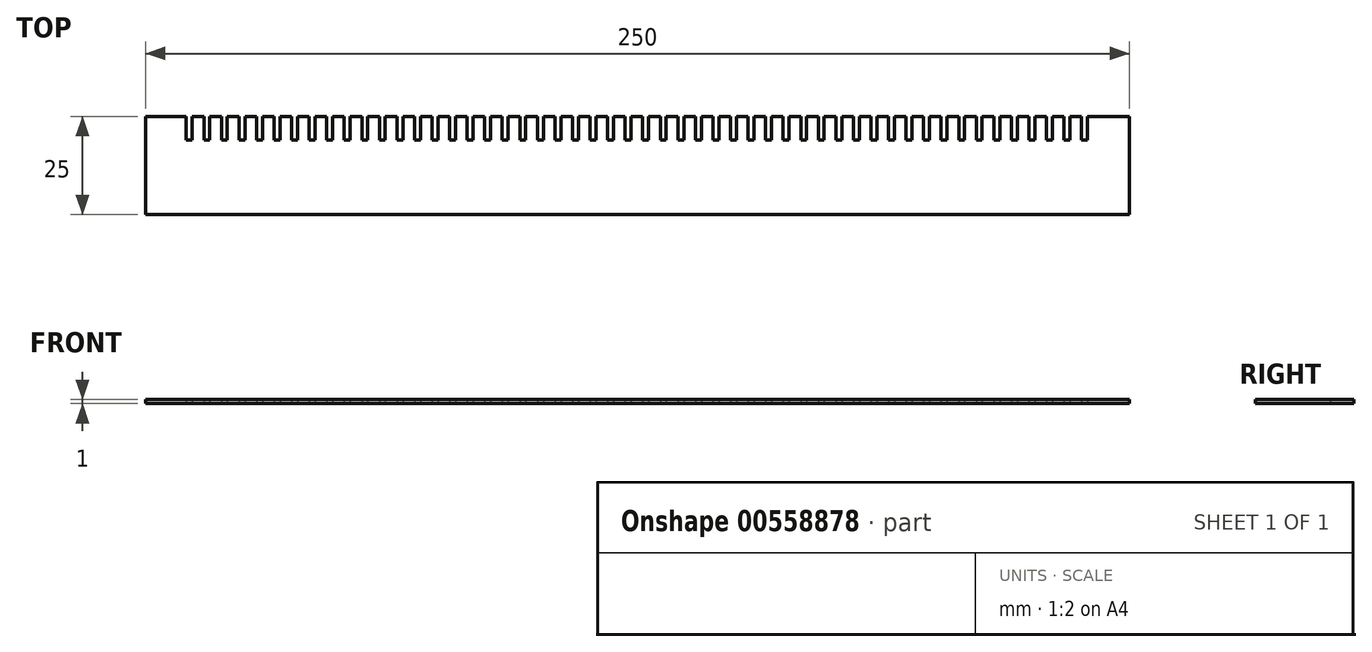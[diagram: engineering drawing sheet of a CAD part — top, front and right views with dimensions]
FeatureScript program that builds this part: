
annotation { "Feature Type Name" : "Feature", "Feature Type Description" : "" }
export const myFeature = defineFeature(function(context is Context, id is Id, definition is map)
    precondition{}
    {
        {
            var Q0;
            Q0=qCreatedBy(makeId("Top.planeOp"),FACE);
            var sketch = newSketch(context, id + "F0", { "sketchPlane" : qUnion([Q0])});
            skLineSegment(sketch, "E0.bottom", {"start": v(-82.75, 53.01) * mm, "end": v(-72.35, 53.01) * mm});
            skLineSegment(sketch, "E0.top", {"start": v(-82.75, 28.01) * mm, "end": v(167.25, 28.01) * mm});
            skLineSegment(sketch, "E0.left", {"start": v(-82.75, 53.01) * mm, "end": v(-82.75, 28.01) * mm});
            skLineSegment(sketch, "E0.right", {"start": v(167.25, 53.01) * mm, "end": v(167.25, 28.01) * mm});
            skLineSegment(sketch, "E1.top", {"start": v(-72.35, 47.01) * mm, "end": v(-70.85, 47.01) * mm});
            skLineSegment(sketch, "E1.left", {"start": v(-72.35, 53.01) * mm, "end": v(-72.35, 47.01) * mm});
            skLineSegment(sketch, "E1.right", {"start": v(-70.85, 53.01) * mm, "end": v(-70.85, 47.01) * mm});
            skLineSegment(sketch, "E2.trimOffspring", {"start": v(-70.85, 53.01) * mm, "end": v(-67.9, 53.01) * mm});
            skLineSegment(sketch, "E3.1.0.0", {"start": v(-67.9, 47.01) * mm, "end": v(-66.4, 47.01) * mm});
            skLineSegment(sketch, "E3.1.0.1", {"start": v(-67.9, 53.01) * mm, "end": v(-67.9, 47.01) * mm});
            skLineSegment(sketch, "E3.1.0.2", {"start": v(-66.4, 53.01) * mm, "end": v(-66.4, 47.01) * mm});
            skLineSegment(sketch, "E3.2.0.0", {"start": v(-63.43, 47.01) * mm, "end": v(-61.93, 47.01) * mm});
            skLineSegment(sketch, "E3.2.0.1", {"start": v(-63.43, 53.01) * mm, "end": v(-63.43, 47.01) * mm});
            skLineSegment(sketch, "E3.2.0.2", {"start": v(-61.93, 53.01) * mm, "end": v(-61.93, 47.01) * mm});
            skLineSegment(sketch, "E3.3.0.0", {"start": v(-58.97, 47.01) * mm, "end": v(-57.47, 47.01) * mm});
            skLineSegment(sketch, "E3.3.0.1", {"start": v(-58.97, 53.01) * mm, "end": v(-58.97, 47.01) * mm});
            skLineSegment(sketch, "E3.3.0.2", {"start": v(-57.47, 53.01) * mm, "end": v(-57.47, 47.01) * mm});
            skLineSegment(sketch, "E3.4.0.0", {"start": v(-54.51, 47.01) * mm, "end": v(-53.01, 47.01) * mm});
            skLineSegment(sketch, "E3.4.0.1", {"start": v(-54.51, 53.01) * mm, "end": v(-54.51, 47.01) * mm});
            skLineSegment(sketch, "E3.4.0.2", {"start": v(-53.01, 53.01) * mm, "end": v(-53.01, 47.01) * mm});
            skLineSegment(sketch, "E3.5.0.0", {"start": v(-50.05, 47.01) * mm, "end": v(-48.55, 47.01) * mm});
            skLineSegment(sketch, "E3.5.0.1", {"start": v(-50.05, 53.01) * mm, "end": v(-50.05, 47.01) * mm});
            skLineSegment(sketch, "E3.5.0.2", {"start": v(-48.55, 53.01) * mm, "end": v(-48.55, 47.01) * mm});
            skLineSegment(sketch, "E3.6.0.0", {"start": v(-45.6, 47.01) * mm, "end": v(-44.1, 47.01) * mm});
            skLineSegment(sketch, "E3.6.0.1", {"start": v(-45.6, 53.01) * mm, "end": v(-45.6, 47.01) * mm});
            skLineSegment(sketch, "E3.6.0.2", {"start": v(-44.1, 53.01) * mm, "end": v(-44.1, 47.01) * mm});
            skLineSegment(sketch, "E3.7.0.0", {"start": v(-41.13, 47.01) * mm, "end": v(-39.63, 47.01) * mm});
            skLineSegment(sketch, "E3.7.0.1", {"start": v(-41.13, 53.01) * mm, "end": v(-41.13, 47.01) * mm});
            skLineSegment(sketch, "E3.7.0.2", {"start": v(-39.63, 53.01) * mm, "end": v(-39.63, 47.01) * mm});
            skLineSegment(sketch, "E3.8.0.0", {"start": v(-36.67, 47.01) * mm, "end": v(-35.17, 47.01) * mm});
            skLineSegment(sketch, "E3.8.0.1", {"start": v(-36.67, 53.01) * mm, "end": v(-36.67, 47.01) * mm});
            skLineSegment(sketch, "E3.8.0.2", {"start": v(-35.17, 53.01) * mm, "end": v(-35.17, 47.01) * mm});
            skLineSegment(sketch, "E3.9.0.0", {"start": v(-32.21, 47.01) * mm, "end": v(-30.71, 47.01) * mm});
            skLineSegment(sketch, "E3.9.0.1", {"start": v(-32.21, 53.01) * mm, "end": v(-32.21, 47.01) * mm});
            skLineSegment(sketch, "E3.9.0.2", {"start": v(-30.71, 53.01) * mm, "end": v(-30.71, 47.01) * mm});
            skLineSegment(sketch, "E3.10.0.0", {"start": v(-27.75, 47.01) * mm, "end": v(-26.25, 47.01) * mm});
            skLineSegment(sketch, "E3.10.0.1", {"start": v(-27.75, 53.01) * mm, "end": v(-27.75, 47.01) * mm});
            skLineSegment(sketch, "E3.10.0.2", {"start": v(-26.25, 53.01) * mm, "end": v(-26.25, 47.01) * mm});
            skLineSegment(sketch, "E3.11.0.0", {"start": v(-23.3, 47.01) * mm, "end": v(-21.8, 47.01) * mm});
            skLineSegment(sketch, "E3.11.0.1", {"start": v(-23.3, 53.01) * mm, "end": v(-23.3, 47.01) * mm});
            skLineSegment(sketch, "E3.11.0.2", {"start": v(-21.8, 53.01) * mm, "end": v(-21.8, 47.01) * mm});
            skLineSegment(sketch, "E3.12.0.0", {"start": v(-18.83, 47.01) * mm, "end": v(-17.33, 47.01) * mm});
            skLineSegment(sketch, "E3.12.0.1", {"start": v(-18.83, 53.01) * mm, "end": v(-18.83, 47.01) * mm});
            skLineSegment(sketch, "E3.12.0.2", {"start": v(-17.33, 53.01) * mm, "end": v(-17.33, 47.01) * mm});
            skLineSegment(sketch, "E3.13.0.0", {"start": v(-14.37, 47.01) * mm, "end": v(-12.87, 47.01) * mm});
            skLineSegment(sketch, "E3.13.0.1", {"start": v(-14.37, 53.01) * mm, "end": v(-14.37, 47.01) * mm});
            skLineSegment(sketch, "E3.13.0.2", {"start": v(-12.87, 53.01) * mm, "end": v(-12.87, 47.01) * mm});
            skLineSegment(sketch, "E3.14.0.0", {"start": v(-9.91, 47.01) * mm, "end": v(-8.41, 47.01) * mm});
            skLineSegment(sketch, "E3.14.0.1", {"start": v(-9.91, 53.01) * mm, "end": v(-9.91, 47.01) * mm});
            skLineSegment(sketch, "E3.14.0.2", {"start": v(-8.41, 53.01) * mm, "end": v(-8.41, 47.01) * mm});
            skLineSegment(sketch, "E3.15.0.0", {"start": v(-5.45, 47.01) * mm, "end": v(-3.95, 47.01) * mm});
            skLineSegment(sketch, "E3.15.0.1", {"start": v(-5.45, 53.01) * mm, "end": v(-5.45, 47.01) * mm});
            skLineSegment(sketch, "E3.15.0.2", {"start": v(-3.95, 53.01) * mm, "end": v(-3.95, 47.01) * mm});
            skLineSegment(sketch, "E3.16.0.0", {"start": v(-1, 47.01) * mm, "end": v(0.5, 47.01) * mm});
            skLineSegment(sketch, "E3.16.0.1", {"start": v(-1, 53.01) * mm, "end": v(-1, 47.01) * mm});
            skLineSegment(sketch, "E3.16.0.2", {"start": v(0.5, 53.01) * mm, "end": v(0.5, 47.01) * mm});
            skLineSegment(sketch, "E3.17.0.0", {"start": v(3.47, 47.01) * mm, "end": v(4.97, 47.01) * mm});
            skLineSegment(sketch, "E3.17.0.1", {"start": v(3.47, 53.01) * mm, "end": v(3.47, 47.01) * mm});
            skLineSegment(sketch, "E3.17.0.2", {"start": v(4.97, 53.01) * mm, "end": v(4.97, 47.01) * mm});
            skLineSegment(sketch, "E3.18.0.0", {"start": v(7.93, 47.01) * mm, "end": v(9.43, 47.01) * mm});
            skLineSegment(sketch, "E3.18.0.1", {"start": v(7.93, 53.01) * mm, "end": v(7.93, 47.01) * mm});
            skLineSegment(sketch, "E3.18.0.2", {"start": v(9.43, 53.01) * mm, "end": v(9.43, 47.01) * mm});
            skLineSegment(sketch, "E3.19.0.0", {"start": v(12.39, 47.01) * mm, "end": v(13.89, 47.01) * mm});
            skLineSegment(sketch, "E3.19.0.1", {"start": v(12.39, 53.01) * mm, "end": v(12.39, 47.01) * mm});
            skLineSegment(sketch, "E3.19.0.2", {"start": v(13.89, 53.01) * mm, "end": v(13.89, 47.01) * mm});
            skLineSegment(sketch, "E3.20.0.0", {"start": v(16.85, 47.01) * mm, "end": v(18.35, 47.01) * mm});
            skLineSegment(sketch, "E3.20.0.1", {"start": v(16.85, 53.01) * mm, "end": v(16.85, 47.01) * mm});
            skLineSegment(sketch, "E3.20.0.2", {"start": v(18.35, 53.01) * mm, "end": v(18.35, 47.01) * mm});
            skLineSegment(sketch, "E3.21.0.0", {"start": v(21.3, 47.01) * mm, "end": v(22.8, 47.01) * mm});
            skLineSegment(sketch, "E3.21.0.1", {"start": v(21.3, 53.01) * mm, "end": v(21.3, 47.01) * mm});
            skLineSegment(sketch, "E3.21.0.2", {"start": v(22.8, 53.01) * mm, "end": v(22.8, 47.01) * mm});
            skLineSegment(sketch, "E3.22.0.0", {"start": v(25.77, 47.01) * mm, "end": v(27.27, 47.01) * mm});
            skLineSegment(sketch, "E3.22.0.1", {"start": v(25.77, 53.01) * mm, "end": v(25.77, 47.01) * mm});
            skLineSegment(sketch, "E3.22.0.2", {"start": v(27.27, 53.01) * mm, "end": v(27.27, 47.01) * mm});
            skLineSegment(sketch, "E3.23.0.0", {"start": v(30.23, 47.01) * mm, "end": v(31.73, 47.01) * mm});
            skLineSegment(sketch, "E3.23.0.1", {"start": v(30.23, 53.01) * mm, "end": v(30.23, 47.01) * mm});
            skLineSegment(sketch, "E3.23.0.2", {"start": v(31.73, 53.01) * mm, "end": v(31.73, 47.01) * mm});
            skLineSegment(sketch, "E3.24.0.0", {"start": v(34.69, 47.01) * mm, "end": v(36.19, 47.01) * mm});
            skLineSegment(sketch, "E3.24.0.1", {"start": v(34.69, 53.01) * mm, "end": v(34.69, 47.01) * mm});
            skLineSegment(sketch, "E3.24.0.2", {"start": v(36.19, 53.01) * mm, "end": v(36.19, 47.01) * mm});
            skLineSegment(sketch, "E3.25.0.0", {"start": v(39.15, 47.01) * mm, "end": v(40.65, 47.01) * mm});
            skLineSegment(sketch, "E3.25.0.1", {"start": v(39.15, 53.01) * mm, "end": v(39.15, 47.01) * mm});
            skLineSegment(sketch, "E3.25.0.2", {"start": v(40.65, 53.01) * mm, "end": v(40.65, 47.01) * mm});
            skLineSegment(sketch, "E3.26.0.0", {"start": v(43.6, 47.01) * mm, "end": v(45.1, 47.01) * mm});
            skLineSegment(sketch, "E3.26.0.1", {"start": v(43.6, 53.01) * mm, "end": v(43.6, 47.01) * mm});
            skLineSegment(sketch, "E3.26.0.2", {"start": v(45.1, 53.01) * mm, "end": v(45.1, 47.01) * mm});
            skLineSegment(sketch, "E3.27.0.0", {"start": v(48.07, 47.01) * mm, "end": v(49.57, 47.01) * mm});
            skLineSegment(sketch, "E3.27.0.1", {"start": v(48.07, 53.01) * mm, "end": v(48.07, 47.01) * mm});
            skLineSegment(sketch, "E3.27.0.2", {"start": v(49.57, 53.01) * mm, "end": v(49.57, 47.01) * mm});
            skLineSegment(sketch, "E3.28.0.0", {"start": v(52.53, 47.01) * mm, "end": v(54.03, 47.01) * mm});
            skLineSegment(sketch, "E3.28.0.1", {"start": v(52.53, 53.01) * mm, "end": v(52.53, 47.01) * mm});
            skLineSegment(sketch, "E3.28.0.2", {"start": v(54.03, 53.01) * mm, "end": v(54.03, 47.01) * mm});
            skLineSegment(sketch, "E3.29.0.0", {"start": v(56.99, 47.01) * mm, "end": v(58.49, 47.01) * mm});
            skLineSegment(sketch, "E3.29.0.1", {"start": v(56.99, 53.01) * mm, "end": v(56.99, 47.01) * mm});
            skLineSegment(sketch, "E3.29.0.2", {"start": v(58.49, 53.01) * mm, "end": v(58.49, 47.01) * mm});
            skLineSegment(sketch, "E3.direction1", {"start": v(-72.35, 47.01) * mm, "end": v(-67.9, 47.01) * mm, "construction": true});
            skLineSegment(sketch, "E4.trimOffspring", {"start": v(-66.4, 53.01) * mm, "end": v(-63.43, 53.01) * mm});
            skLineSegment(sketch, "E5.trimOffspring", {"start": v(-61.93, 53.01) * mm, "end": v(-58.97, 53.01) * mm});
            skLineSegment(sketch, "E6.trimOffspring", {"start": v(-57.47, 53.01) * mm, "end": v(-54.51, 53.01) * mm});
            skLineSegment(sketch, "E7.trimOffspring", {"start": v(-53.01, 53.01) * mm, "end": v(-50.05, 53.01) * mm});
            skLineSegment(sketch, "E8.trimOffspring", {"start": v(-48.55, 53.01) * mm, "end": v(-45.6, 53.01) * mm});
            skLineSegment(sketch, "E9.trimOffspring", {"start": v(-44.1, 53.01) * mm, "end": v(-41.13, 53.01) * mm});
            skLineSegment(sketch, "E10.trimOffspring", {"start": v(-39.63, 53.01) * mm, "end": v(-36.67, 53.01) * mm});
            skLineSegment(sketch, "E11.trimOffspring", {"start": v(-35.17, 53.01) * mm, "end": v(-32.21, 53.01) * mm});
            skLineSegment(sketch, "E12.trimOffspring", {"start": v(-30.71, 53.01) * mm, "end": v(-27.75, 53.01) * mm});
            skLineSegment(sketch, "E13.1.0.0", {"start": v(61.45, 53.01) * mm, "end": v(61.45, 47.01) * mm});
            skLineSegment(sketch, "E13.1.0.1", {"start": v(61.45, 47.01) * mm, "end": v(62.95, 47.01) * mm});
            skLineSegment(sketch, "E13.1.0.2", {"start": v(62.95, 53.01) * mm, "end": v(62.95, 47.01) * mm});
            skLineSegment(sketch, "E13.2.0.0", {"start": v(65.9, 53.01) * mm, "end": v(65.9, 47.01) * mm});
            skLineSegment(sketch, "E13.2.0.1", {"start": v(65.9, 47.01) * mm, "end": v(67.4, 47.01) * mm});
            skLineSegment(sketch, "E13.2.0.2", {"start": v(67.4, 53.01) * mm, "end": v(67.4, 47.01) * mm});
            skLineSegment(sketch, "E13.3.0.0", {"start": v(70.37, 53.01) * mm, "end": v(70.37, 47.01) * mm});
            skLineSegment(sketch, "E13.3.0.1", {"start": v(70.37, 47.01) * mm, "end": v(71.87, 47.01) * mm});
            skLineSegment(sketch, "E13.3.0.2", {"start": v(71.87, 53.01) * mm, "end": v(71.87, 47.01) * mm});
            skLineSegment(sketch, "E13.4.0.0", {"start": v(74.83, 53.01) * mm, "end": v(74.83, 47.01) * mm});
            skLineSegment(sketch, "E13.4.0.1", {"start": v(74.83, 47.01) * mm, "end": v(76.33, 47.01) * mm});
            skLineSegment(sketch, "E13.4.0.2", {"start": v(76.33, 53.01) * mm, "end": v(76.33, 47.01) * mm});
            skLineSegment(sketch, "E13.5.0.0", {"start": v(79.29, 53.01) * mm, "end": v(79.29, 47.01) * mm});
            skLineSegment(sketch, "E13.5.0.1", {"start": v(79.29, 47.01) * mm, "end": v(80.79, 47.01) * mm});
            skLineSegment(sketch, "E13.5.0.2", {"start": v(80.79, 53.01) * mm, "end": v(80.79, 47.01) * mm});
            skLineSegment(sketch, "E13.6.0.0", {"start": v(83.75, 53.01) * mm, "end": v(83.75, 47.01) * mm});
            skLineSegment(sketch, "E13.6.0.1", {"start": v(83.75, 47.01) * mm, "end": v(85.25, 47.01) * mm});
            skLineSegment(sketch, "E13.6.0.2", {"start": v(85.25, 53.01) * mm, "end": v(85.25, 47.01) * mm});
            skLineSegment(sketch, "E13.7.0.0", {"start": v(88.2, 53.01) * mm, "end": v(88.2, 47.01) * mm});
            skLineSegment(sketch, "E13.7.0.1", {"start": v(88.2, 47.01) * mm, "end": v(89.7, 47.01) * mm});
            skLineSegment(sketch, "E13.7.0.2", {"start": v(89.7, 53.01) * mm, "end": v(89.7, 47.01) * mm});
            skLineSegment(sketch, "E13.8.0.0", {"start": v(92.67, 53.01) * mm, "end": v(92.67, 47.01) * mm});
            skLineSegment(sketch, "E13.8.0.1", {"start": v(92.67, 47.01) * mm, "end": v(94.17, 47.01) * mm});
            skLineSegment(sketch, "E13.8.0.2", {"start": v(94.17, 53.01) * mm, "end": v(94.17, 47.01) * mm});
            skLineSegment(sketch, "E13.9.0.0", {"start": v(97.13, 53.01) * mm, "end": v(97.13, 47.01) * mm});
            skLineSegment(sketch, "E13.9.0.1", {"start": v(97.13, 47.01) * mm, "end": v(98.63, 47.01) * mm});
            skLineSegment(sketch, "E13.9.0.2", {"start": v(98.63, 53.01) * mm, "end": v(98.63, 47.01) * mm});
            skLineSegment(sketch, "E13.10.0.0", {"start": v(101.59, 53.01) * mm, "end": v(101.59, 47.01) * mm});
            skLineSegment(sketch, "E13.10.0.1", {"start": v(101.59, 47.01) * mm, "end": v(103.09, 47.01) * mm});
            skLineSegment(sketch, "E13.10.0.2", {"start": v(103.09, 53.01) * mm, "end": v(103.09, 47.01) * mm});
            skLineSegment(sketch, "E13.11.0.0", {"start": v(106.05, 53.01) * mm, "end": v(106.05, 47.01) * mm});
            skLineSegment(sketch, "E13.11.0.1", {"start": v(106.05, 47.01) * mm, "end": v(107.55, 47.01) * mm});
            skLineSegment(sketch, "E13.11.0.2", {"start": v(107.55, 53.01) * mm, "end": v(107.55, 47.01) * mm});
            skLineSegment(sketch, "E13.12.0.0", {"start": v(110.5, 53.01) * mm, "end": v(110.5, 47.01) * mm});
            skLineSegment(sketch, "E13.12.0.1", {"start": v(110.5, 47.01) * mm, "end": v(112, 47.01) * mm});
            skLineSegment(sketch, "E13.12.0.2", {"start": v(112, 53.01) * mm, "end": v(112, 47.01) * mm});
            skLineSegment(sketch, "E13.13.0.0", {"start": v(114.97, 53.01) * mm, "end": v(114.97, 47.01) * mm});
            skLineSegment(sketch, "E13.13.0.1", {"start": v(114.97, 47.01) * mm, "end": v(116.47, 47.01) * mm});
            skLineSegment(sketch, "E13.13.0.2", {"start": v(116.47, 53.01) * mm, "end": v(116.47, 47.01) * mm});
            skLineSegment(sketch, "E13.14.0.0", {"start": v(119.43, 53.01) * mm, "end": v(119.43, 47.01) * mm});
            skLineSegment(sketch, "E13.14.0.1", {"start": v(119.43, 47.01) * mm, "end": v(120.93, 47.01) * mm});
            skLineSegment(sketch, "E13.14.0.2", {"start": v(120.93, 53.01) * mm, "end": v(120.93, 47.01) * mm});
            skLineSegment(sketch, "E13.15.0.0", {"start": v(123.89, 53.01) * mm, "end": v(123.89, 47.01) * mm});
            skLineSegment(sketch, "E13.15.0.1", {"start": v(123.89, 47.01) * mm, "end": v(125.39, 47.01) * mm});
            skLineSegment(sketch, "E13.15.0.2", {"start": v(125.39, 53.01) * mm, "end": v(125.39, 47.01) * mm});
            skLineSegment(sketch, "E13.16.0.0", {"start": v(128.35, 53.01) * mm, "end": v(128.35, 47.01) * mm});
            skLineSegment(sketch, "E13.16.0.1", {"start": v(128.35, 47.01) * mm, "end": v(129.85, 47.01) * mm});
            skLineSegment(sketch, "E13.16.0.2", {"start": v(129.85, 53.01) * mm, "end": v(129.85, 47.01) * mm});
            skLineSegment(sketch, "E13.17.0.0", {"start": v(132.8, 53.01) * mm, "end": v(132.8, 47.01) * mm});
            skLineSegment(sketch, "E13.17.0.1", {"start": v(132.8, 47.01) * mm, "end": v(134.3, 47.01) * mm});
            skLineSegment(sketch, "E13.17.0.2", {"start": v(134.3, 53.01) * mm, "end": v(134.3, 47.01) * mm});
            skLineSegment(sketch, "E13.18.0.0", {"start": v(137.27, 53.01) * mm, "end": v(137.27, 47.01) * mm});
            skLineSegment(sketch, "E13.18.0.1", {"start": v(137.27, 47.01) * mm, "end": v(138.77, 47.01) * mm});
            skLineSegment(sketch, "E13.18.0.2", {"start": v(138.77, 53.01) * mm, "end": v(138.77, 47.01) * mm});
            skLineSegment(sketch, "E13.19.0.0", {"start": v(141.73, 53.01) * mm, "end": v(141.73, 47.01) * mm});
            skLineSegment(sketch, "E13.19.0.1", {"start": v(141.73, 47.01) * mm, "end": v(143.23, 47.01) * mm});
            skLineSegment(sketch, "E13.19.0.2", {"start": v(143.23, 53.01) * mm, "end": v(143.23, 47.01) * mm});
            skLineSegment(sketch, "E13.20.0.0", {"start": v(146.19, 53.01) * mm, "end": v(146.19, 47.01) * mm});
            skLineSegment(sketch, "E13.20.0.1", {"start": v(146.19, 47.01) * mm, "end": v(147.69, 47.01) * mm});
            skLineSegment(sketch, "E13.20.0.2", {"start": v(147.69, 53.01) * mm, "end": v(147.69, 47.01) * mm});
            skLineSegment(sketch, "E13.21.0.0", {"start": v(150.65, 53.01) * mm, "end": v(150.65, 47.01) * mm});
            skLineSegment(sketch, "E13.21.0.1", {"start": v(150.65, 47.01) * mm, "end": v(152.15, 47.01) * mm});
            skLineSegment(sketch, "E13.21.0.2", {"start": v(152.15, 53.01) * mm, "end": v(152.15, 47.01) * mm});
            skLineSegment(sketch, "E13.22.0.0", {"start": v(155.1, 53.01) * mm, "end": v(155.1, 47.01) * mm});
            skLineSegment(sketch, "E13.22.0.1", {"start": v(155.1, 47.01) * mm, "end": v(156.6, 47.01) * mm});
            skLineSegment(sketch, "E13.22.0.2", {"start": v(156.6, 53.01) * mm, "end": v(156.6, 47.01) * mm});
            skLineSegment(sketch, "E13.direction1", {"start": v(56.99, 47.01) * mm, "end": v(61.45, 47.01) * mm, "construction": true});
            skLineSegment(sketch, "E14.trimOffspring", {"start": v(-8.41, 53.01) * mm, "end": v(-5.45, 53.01) * mm});
            skLineSegment(sketch, "E15.trimOffspring", {"start": v(-12.87, 53.01) * mm, "end": v(-9.91, 53.01) * mm});
            skLineSegment(sketch, "E16.trimOffspring", {"start": v(-17.33, 53.01) * mm, "end": v(-14.37, 53.01) * mm});
            skLineSegment(sketch, "E17.trimOffspring", {"start": v(-21.8, 53.01) * mm, "end": v(-18.83, 53.01) * mm});
            skLineSegment(sketch, "E18.trimOffspring", {"start": v(-3.95, 53.01) * mm, "end": v(-1, 53.01) * mm});
            skLineSegment(sketch, "E19.trimOffspring", {"start": v(0.5, 53.01) * mm, "end": v(3.47, 53.01) * mm});
            skLineSegment(sketch, "E20.trimOffspring", {"start": v(4.97, 53.01) * mm, "end": v(7.93, 53.01) * mm});
            skLineSegment(sketch, "E21.trimOffspring", {"start": v(-26.25, 53.01) * mm, "end": v(-23.3, 53.01) * mm});
            skLineSegment(sketch, "E22.trimOffspring", {"start": v(9.43, 53.01) * mm, "end": v(12.39, 53.01) * mm});
            skLineSegment(sketch, "E23.trimOffspring", {"start": v(13.89, 53.01) * mm, "end": v(16.85, 53.01) * mm});
            skLineSegment(sketch, "E24.trimOffspring", {"start": v(18.35, 53.01) * mm, "end": v(21.3, 53.01) * mm});
            skLineSegment(sketch, "E25.trimOffspring", {"start": v(22.8, 53.01) * mm, "end": v(25.77, 53.01) * mm});
            skLineSegment(sketch, "E26.trimOffspring", {"start": v(27.27, 53.01) * mm, "end": v(30.23, 53.01) * mm});
            skLineSegment(sketch, "E27.trimOffspring", {"start": v(31.73, 53.01) * mm, "end": v(34.69, 53.01) * mm});
            skLineSegment(sketch, "E28.trimOffspring", {"start": v(36.19, 53.01) * mm, "end": v(39.15, 53.01) * mm});
            skLineSegment(sketch, "E29.trimOffspring", {"start": v(40.65, 53.01) * mm, "end": v(43.6, 53.01) * mm});
            skLineSegment(sketch, "E30.trimOffspring", {"start": v(45.1, 53.01) * mm, "end": v(48.07, 53.01) * mm});
            skLineSegment(sketch, "E31.trimOffspring", {"start": v(49.57, 53.01) * mm, "end": v(52.53, 53.01) * mm});
            skLineSegment(sketch, "E32.trimOffspring", {"start": v(54.03, 53.01) * mm, "end": v(56.99, 53.01) * mm});
            skLineSegment(sketch, "E33.trimOffspring", {"start": v(58.49, 53.01) * mm, "end": v(61.45, 53.01) * mm});
            skLineSegment(sketch, "E34.trimOffspring", {"start": v(62.95, 53.01) * mm, "end": v(65.9, 53.01) * mm});
            skLineSegment(sketch, "E35.trimOffspring", {"start": v(67.4, 53.01) * mm, "end": v(70.37, 53.01) * mm});
            skLineSegment(sketch, "E36.trimOffspring", {"start": v(71.87, 53.01) * mm, "end": v(74.83, 53.01) * mm});
            skLineSegment(sketch, "E37.trimOffspring", {"start": v(76.33, 53.01) * mm, "end": v(79.29, 53.01) * mm});
            skLineSegment(sketch, "E38.trimOffspring", {"start": v(80.79, 53.01) * mm, "end": v(83.75, 53.01) * mm});
            skLineSegment(sketch, "E39.trimOffspring", {"start": v(85.25, 53.01) * mm, "end": v(88.2, 53.01) * mm});
            skLineSegment(sketch, "E40.trimOffspring", {"start": v(89.7, 53.01) * mm, "end": v(92.67, 53.01) * mm});
            skLineSegment(sketch, "E41.trimOffspring", {"start": v(94.17, 53.01) * mm, "end": v(97.13, 53.01) * mm});
            skLineSegment(sketch, "E42.trimOffspring", {"start": v(98.63, 53.01) * mm, "end": v(101.59, 53.01) * mm});
            skLineSegment(sketch, "E43.trimOffspring", {"start": v(103.09, 53.01) * mm, "end": v(106.05, 53.01) * mm});
            skLineSegment(sketch, "E44.trimOffspring", {"start": v(107.55, 53.01) * mm, "end": v(110.5, 53.01) * mm});
            skLineSegment(sketch, "E45.trimOffspring", {"start": v(112, 53.01) * mm, "end": v(114.97, 53.01) * mm});
            skLineSegment(sketch, "E46.trimOffspring", {"start": v(116.47, 53.01) * mm, "end": v(119.43, 53.01) * mm});
            skLineSegment(sketch, "E47.trimOffspring", {"start": v(120.93, 53.01) * mm, "end": v(123.89, 53.01) * mm});
            skLineSegment(sketch, "E48.trimOffspring", {"start": v(125.39, 53.01) * mm, "end": v(128.35, 53.01) * mm});
            skLineSegment(sketch, "E49.trimOffspring", {"start": v(129.85, 53.01) * mm, "end": v(132.8, 53.01) * mm});
            skLineSegment(sketch, "E50.trimOffspring", {"start": v(134.3, 53.01) * mm, "end": v(137.27, 53.01) * mm});
            skLineSegment(sketch, "E51.trimOffspring", {"start": v(138.77, 53.01) * mm, "end": v(141.73, 53.01) * mm});
            skLineSegment(sketch, "E52.trimOffspring", {"start": v(143.23, 53.01) * mm, "end": v(146.19, 53.01) * mm});
            skLineSegment(sketch, "E53.trimOffspring", {"start": v(147.69, 53.01) * mm, "end": v(150.65, 53.01) * mm});
            skLineSegment(sketch, "E54.trimOffspring", {"start": v(152.15, 53.01) * mm, "end": v(155.1, 53.01) * mm});
            skLineSegment(sketch, "E55.trimOffspring", {"start": v(156.6, 53.01) * mm, "end": v(167.25, 53.01) * mm});
            skSolve(sketch);
        }
        {
            var Q0;
            Q0=makeQuery(id+"F0.imprint","IMPRINT",FACE,{"disambiguationData":[TD([[makeQuery(id+"F0.imprint","IMPRINT",EDGE,{"derivedFrom":sQuery(id+"F0.wireOp",EDGE,"E0.bottom")}),-1.0]])]});
            extrude(context, id + "F1", {"entities" : qUnion([Q0]), "depth" : 1 * mm, "offsetDistance" : 25 * mm});
        }
    });
